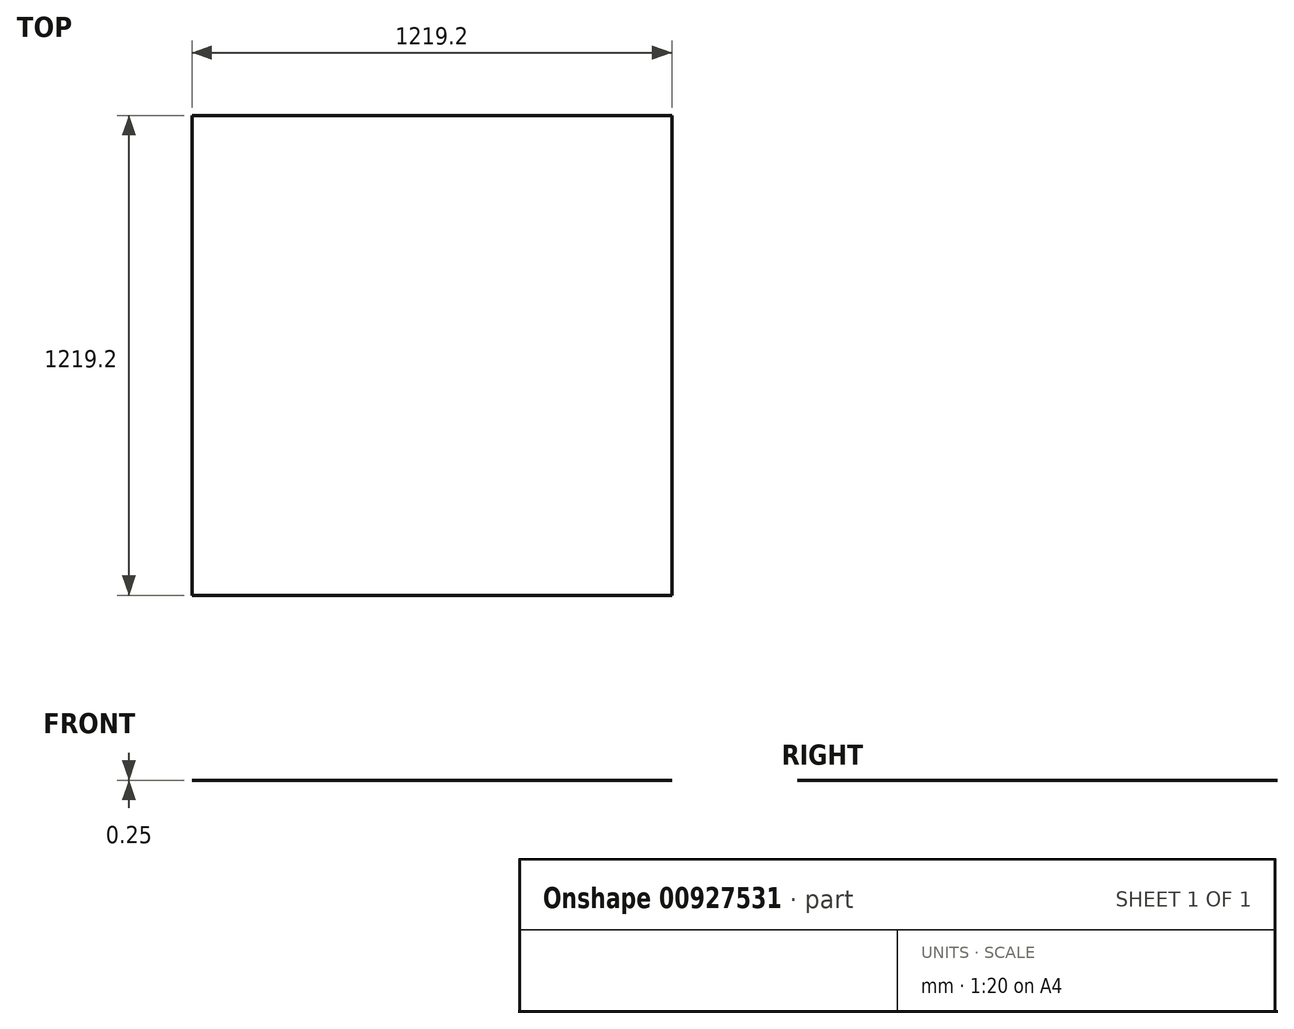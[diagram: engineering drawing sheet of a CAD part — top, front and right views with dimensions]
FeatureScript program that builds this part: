
annotation { "Feature Type Name" : "Feature", "Feature Type Description" : "" }
export const myFeature = defineFeature(function(context is Context, id is Id, definition is map)
    precondition{}
    {
        {
            var Q0;
            Q0=qCreatedBy(makeId("Top.planeOp"),FACE);
            var sketch = newSketch(context, id + "F0", { "sketchPlane" : qUnion([Q0])});
            skLineSegment(sketch, "E0.bottom", {"start": v(-605.67, 889.94) * mm, "end": v(613.53, 889.94) * mm});
            skLineSegment(sketch, "E0.top", {"start": v(-605.67, -329.26) * mm, "end": v(613.53, -329.26) * mm});
            skLineSegment(sketch, "E0.left", {"start": v(-605.67, 889.94) * mm, "end": v(-605.67, -329.26) * mm});
            skLineSegment(sketch, "E0.right", {"start": v(613.53, 889.94) * mm, "end": v(613.53, -329.26) * mm});
            skSolve(sketch);
        }
        {
            var Q0;
            Q0=makeQuery(id+"F0.imprint","IMPRINT",FACE,{"disambiguationData":[TD([[makeQuery(id+"F0.imprint","IMPRINT",EDGE,{"derivedFrom":sQuery(id+"F0.wireOp",EDGE,"E0.bottom")}),-1.0]])]});
            extrude(context, id + "F1", {"entities" : qUnion([Q0]), "depth" : 0.25 * mm, "offsetDistance" : 25.4 * mm});
        }
    });
